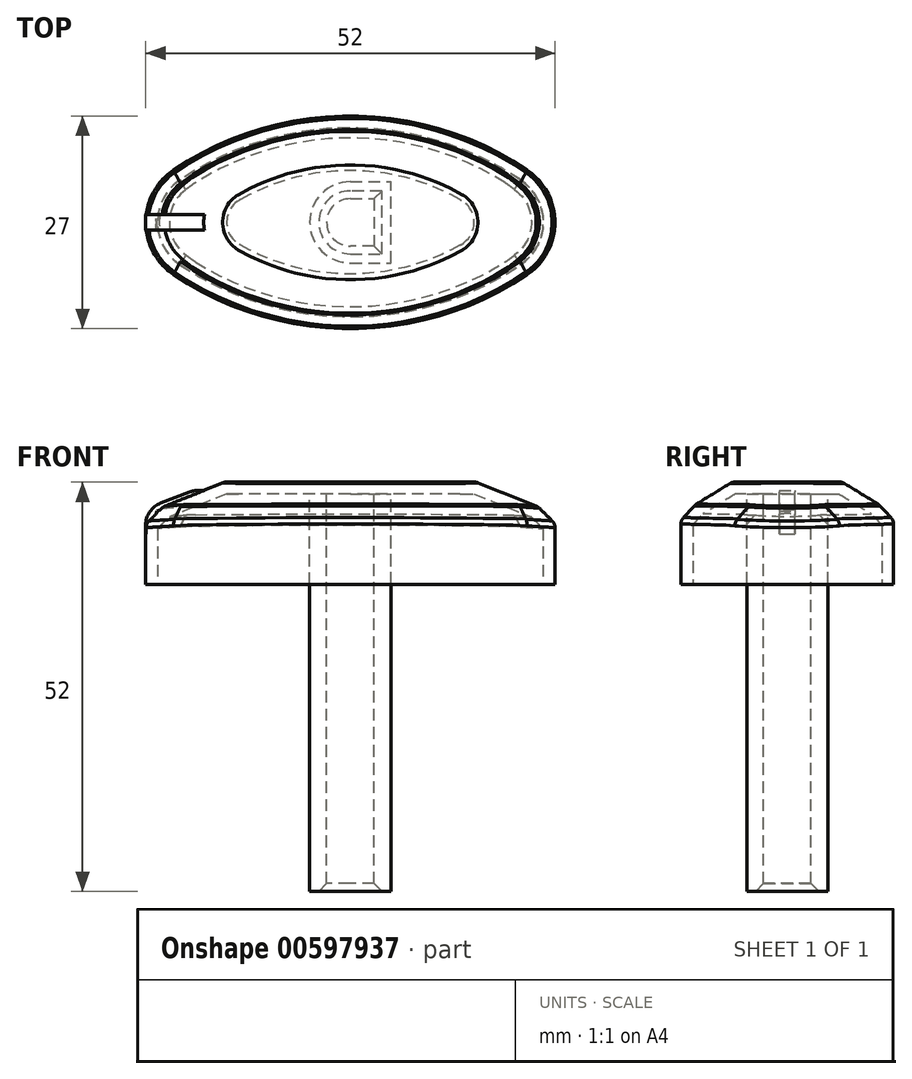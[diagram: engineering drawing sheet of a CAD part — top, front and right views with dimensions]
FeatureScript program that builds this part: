
annotation { "Feature Type Name" : "Feature", "Feature Type Description" : "" }
export const myFeature = defineFeature(function(context is Context, id is Id, definition is map)
    precondition{}
    {
        {
            var Q0;
            Q0=qCreatedBy(makeId("Top.planeOp"),FACE);
            var sketch = newSketch(context, id + "F0", { "sketchPlane" : qUnion([Q0])});
            skLineSegment(sketch, "E0.bottom", {"start": v(26, -13.5) * mm, "end": v(-26, -13.5) * mm, "construction": true});
            skLineSegment(sketch, "E0.top", {"start": v(26, 13.5) * mm, "end": v(-26, 13.5) * mm, "construction": true});
            skLineSegment(sketch, "E0.left", {"start": v(26, -13.5) * mm, "end": v(26, 13.5) * mm, "construction": true});
            skLineSegment(sketch, "E0.right", {"start": v(-26, -13.5) * mm, "end": v(-26, 13.5) * mm, "construction": true});
            skPoint(sketch, "E0.middle", {"position": v(0, 0) * mm});
            skCircle(sketch, "E1", {"center": v(-18, 0) * mm, "radius": 8 * mm});
            skPoint(sketch, "E1.centerSnap0", {"position": v(-26, 0) * mm});
            skCircle(sketch, "E2.MirrorC", {"center": v(18, 0) * mm, "radius": 8 * mm});
            skArc(sketch, "E3", {"start": v(22.47, 6.63) * mm, "mid": v(0, 13.5) * mm, "end": v(-22.47, 6.63) * mm});
            skArc(sketch, "E4.MirrorCS", {"start": v(22.47, -6.63) * mm, "mid": v(0, -13.5) * mm, "end": v(-22.47, -6.63) * mm});
            skSolve(sketch);
        }
        {
            var Q0;
            Q0 = qSketchRegion(id + "F0", true);
            extrude(context, id + "F1", {"entities" : qUnion([Q0]), "depth" : 9 * mm, "offsetDistance" : 25 * mm});
        }
        {
            var Q0;
            Q0=qCreatedBy(makeId("Top.planeOp"),FACE);
            cPlane(context, id + "F2", {"entities" : qUnion([Q0]), "cplaneType" : CPlaneType.OFFSET, "offset" : 13 * mm, "width" : 150 * mm, "height" : 150 * mm});
        }
        {
            var Q0;
            Q0=qCreatedBy(id+"F2.planeOp",FACE);
            var sketch = newSketch(context, id + "F3", { "sketchPlane" : qUnion([Q0])});
            skLineSegment(sketch, "E5.bottom", {"start": v(16, -7) * mm, "end": v(-16, -7) * mm, "construction": true});
            skLineSegment(sketch, "E5.top", {"start": v(16, 7) * mm, "end": v(-16, 7) * mm, "construction": true});
            skLineSegment(sketch, "E5.left", {"start": v(16, -7) * mm, "end": v(16, 7) * mm, "construction": true});
            skLineSegment(sketch, "E5.right", {"start": v(-16, -7) * mm, "end": v(-16, 7) * mm, "construction": true});
            skPoint(sketch, "E5.middle", {"position": v(0, 0) * mm});
            skArc(sketch, "E6", {"start": v(-14.1, 3.26) * mm, "mid": v(-16, 0) * mm, "end": v(-14.1, -3.26) * mm});
            skPoint(sketch, "E6.centerSnap0", {"position": v(-16, 0) * mm});
            skArc(sketch, "E7.MirrorC", {"start": v(14.1, 3.26) * mm, "mid": v(16, 0) * mm, "end": v(14.1, -3.26) * mm});
            skArc(sketch, "E8", {"start": v(14.1, 3.26) * mm, "mid": v(0, 7) * mm, "end": v(-14.1, 3.26) * mm});
            skArc(sketch, "E9.MirrorCS", {"start": v(14.1, -3.26) * mm, "mid": v(0, -7) * mm, "end": v(-14.1, -3.26) * mm});
            skSolve(sketch);
        }
        {
            var Q1;
            Q1=makeQuery(id+"F3.imprint","IMPRINT",FACE,{"disambiguationData":[TD([[makeQuery(id+"F3.imprint","IMPRINT",EDGE,{"derivedFrom":sQuery(id+"F3.wireOp",EDGE,"E6")}),1.0]])]});
            var Q2;
            Q2=makeQuery(id+"F1.opExtrude","CAP_FACE",FACE,{"disambiguationData":[OSD([sQuery(id+"F0.wireOp",EDGE,"E1"),sQuery(id+"F0.wireOp",EDGE,"E2.MirrorC"),sQuery(id+"F0.wireOp",EDGE,"E3"),sQuery(id+"F0.wireOp",EDGE,"E4.MirrorCS")])],"isStart":false});
            loft(context, id + "F4", {"operationType" : NewBodyOperationType.ADD, "sheetProfilesArray" : [{ "sheetProfileEntities" : qUnion([Q1]) }, { "sheetProfileEntities" : qUnion([Q2]) }]});
        }
        {
            var Q0;
            {var subQ0=sQuery(id+"F0.wireOp",EDGE,"E4.MirrorCS");Q0=makeQuery(id+"F4.boolean.opBoolean","MERGE",EDGE,{"derivedFrom":[makeQuery(id+"F1.opExtrude","CAP_EDGE",EDGE,{"disambiguationData":[OSD([subQ0])],"isStart":false}),makeQuery(id+"F4.opLoft","MID_CAP_EDGE",EDGE,{"disambiguationData":[OSD([sQuery(id+"F0.wireOp",EDGE,"E1"),sQuery(id+"F0.wireOp",EDGE,"E2.MirrorC"),subQ0])],"capPos":1.0})]});}
            chamfer(context, id + "F5", {"entities" : qUnion([Q0]), "chamferType" : ChamferType.TWO_OFFSETS, "width1" : 2.2 * mm, "oppositeDirection" : false, "width2" : 1 * mm, "tangentPropagation" : true});
        }
        {
            var Q0;
            {var subQ0=sQuery(id+"F0.wireOp",EDGE,"E2.MirrorC");var subQ1=sQuery(id+"F0.wireOp",EDGE,"E1");var subQ2=sQuery(id+"F0.wireOp",EDGE,"E4.MirrorCS");Q0=makeQuery(id+"F5.opChamfer","BLEND_EDGE",EDGE,{"blendedFrom":[makeQuery(id+"F4.boolean.opBoolean","MERGE",EDGE,{"derivedFrom":[makeQuery(id+"F1.opExtrude","CAP_EDGE",EDGE,{"disambiguationData":[OSD([subQ2])],"isStart":false}),makeQuery(id+"F4.opLoft","MID_CAP_EDGE",EDGE,{"disambiguationData":[OSD([subQ1,subQ0,subQ2])],"capPos":1.0})]}),makeQuery(id+"F4.opLoft","SWEPT_FACE",FACE,{"disambiguationData":[OSD([subQ1,subQ0,sQuery(id+"F0.wireOp",EDGE,"E3"),sQuery(id+"F3.wireOp",EDGE,"E6"),sQuery(id+"F3.wireOp",EDGE,"E7.MirrorC"),sQuery(id+"F3.wireOp",EDGE,"E8")])]})],"blendedInto":[makeQuery(id+"F4.opLoft","SWEPT_FACE",FACE,{"disambiguationData":[OSD([subQ1,subQ0,sQuery(id+"F0.wireOp",EDGE,"E3"),sQuery(id+"F3.wireOp",EDGE,"E6"),sQuery(id+"F3.wireOp",EDGE,"E7.MirrorC"),sQuery(id+"F3.wireOp",EDGE,"E8")])]})]});}
            var Q1;
            {var subQ0=sQuery(id+"F0.wireOp",EDGE,"E4.MirrorCS");Q1=makeQuery(id+"F5.opChamfer","BLEND_EDGE",EDGE,{"blendedFrom":[makeQuery(id+"F4.boolean.opBoolean","MERGE",EDGE,{"derivedFrom":[makeQuery(id+"F1.opExtrude","CAP_EDGE",EDGE,{"disambiguationData":[OSD([subQ0])],"isStart":false}),makeQuery(id+"F4.opLoft","MID_CAP_EDGE",EDGE,{"disambiguationData":[OSD([sQuery(id+"F0.wireOp",EDGE,"E1"),sQuery(id+"F0.wireOp",EDGE,"E2.MirrorC"),subQ0])],"capPos":1.0})]}),makeQuery(id+"F1.opExtrude","SWEPT_FACE",FACE,{"disambiguationData":[OSD([subQ0])]})],"blendedInto":[makeQuery(id+"F1.opExtrude","SWEPT_FACE",FACE,{"disambiguationData":[OSD([subQ0])]})]});}
            var Q2;
            Q2=makeQuery(id+"F4.opLoft","MID_CAP_EDGE",EDGE,{"disambiguationData":[OSD([sQuery(id+"F3.wireOp",EDGE,"E6"),sQuery(id+"F3.wireOp",EDGE,"E7.MirrorC"),sQuery(id+"F3.wireOp",EDGE,"E9.MirrorCS")])],"capPos":0.0});
            var Q3;
            {var subQ0=sQuery(id+"F0.wireOp",EDGE,"E3");var subQ1=sQuery(id+"F0.wireOp",EDGE,"E1");Q3=makeQuery(id+"F5.opChamfer","BLEND_EDGE",EDGE,{"blendedFrom":[makeQuery(id+"F4.boolean.opBoolean","MERGE",EDGE,{"derivedFrom":[makeQuery(id+"F1.opExtrude","CAP_EDGE",EDGE,{"disambiguationData":[OSD([subQ1])],"isStart":false}),makeQuery(id+"F4.opLoft","MID_CAP_EDGE",EDGE,{"disambiguationData":[OSD([subQ1,subQ0,sQuery(id+"F0.wireOp",EDGE,"E4.MirrorCS")])],"capPos":1.0})]}),makeQuery(id+"F4.opLoft","SWEPT_FACE",FACE,{"disambiguationData":[OSD([subQ1,sQuery(id+"F0.wireOp",EDGE,"E2.MirrorC"),subQ0,sQuery(id+"F3.wireOp",EDGE,"E6"),sQuery(id+"F3.wireOp",EDGE,"E7.MirrorC"),sQuery(id+"F3.wireOp",EDGE,"E8")])]})],"blendedInto":[makeQuery(id+"F4.opLoft","SWEPT_FACE",FACE,{"disambiguationData":[OSD([subQ1,sQuery(id+"F0.wireOp",EDGE,"E2.MirrorC"),subQ0,sQuery(id+"F3.wireOp",EDGE,"E6"),sQuery(id+"F3.wireOp",EDGE,"E7.MirrorC"),sQuery(id+"F3.wireOp",EDGE,"E8")])]})]});}
            var Q4;
            {var subQ0=sQuery(id+"F0.wireOp",EDGE,"E1");Q4=makeQuery(id+"F5.opChamfer","BLEND_EDGE",EDGE,{"blendedFrom":[makeQuery(id+"F4.boolean.opBoolean","MERGE",EDGE,{"derivedFrom":[makeQuery(id+"F1.opExtrude","CAP_EDGE",EDGE,{"disambiguationData":[OSD([subQ0])],"isStart":false}),makeQuery(id+"F4.opLoft","MID_CAP_EDGE",EDGE,{"disambiguationData":[OSD([subQ0,sQuery(id+"F0.wireOp",EDGE,"E3"),sQuery(id+"F0.wireOp",EDGE,"E4.MirrorCS")])],"capPos":1.0})]}),makeQuery(id+"F1.opExtrude","SWEPT_FACE",FACE,{"disambiguationData":[OSD([subQ0])]})],"blendedInto":[makeQuery(id+"F1.opExtrude","SWEPT_FACE",FACE,{"disambiguationData":[OSD([subQ0])]})]});}
            var Q5;
            {var subQ0=sQuery(id+"F0.wireOp",EDGE,"E3");var subQ1=sQuery(id+"F0.wireOp",EDGE,"E2.MirrorC");Q5=makeQuery(id+"F5.opChamfer","BLEND_EDGE",EDGE,{"blendedFrom":[makeQuery(id+"F4.boolean.opBoolean","MERGE",EDGE,{"derivedFrom":[makeQuery(id+"F1.opExtrude","CAP_EDGE",EDGE,{"disambiguationData":[OSD([subQ1])],"isStart":false}),makeQuery(id+"F4.opLoft","MID_CAP_EDGE",EDGE,{"disambiguationData":[OSD([subQ1,subQ0,sQuery(id+"F0.wireOp",EDGE,"E4.MirrorCS")])],"capPos":1.0})]}),makeQuery(id+"F4.opLoft","SWEPT_FACE",FACE,{"disambiguationData":[OSD([sQuery(id+"F0.wireOp",EDGE,"E1"),subQ1,subQ0,sQuery(id+"F3.wireOp",EDGE,"E6"),sQuery(id+"F3.wireOp",EDGE,"E7.MirrorC"),sQuery(id+"F3.wireOp",EDGE,"E8")])]})],"blendedInto":[makeQuery(id+"F4.opLoft","SWEPT_FACE",FACE,{"disambiguationData":[OSD([sQuery(id+"F0.wireOp",EDGE,"E1"),subQ1,subQ0,sQuery(id+"F3.wireOp",EDGE,"E6"),sQuery(id+"F3.wireOp",EDGE,"E7.MirrorC"),sQuery(id+"F3.wireOp",EDGE,"E8")])]})]});}
            var Q6;
            {var subQ0=sQuery(id+"F0.wireOp",EDGE,"E2.MirrorC");Q6=makeQuery(id+"F5.opChamfer","BLEND_EDGE",EDGE,{"blendedFrom":[makeQuery(id+"F4.boolean.opBoolean","MERGE",EDGE,{"derivedFrom":[makeQuery(id+"F1.opExtrude","CAP_EDGE",EDGE,{"disambiguationData":[OSD([subQ0])],"isStart":false}),makeQuery(id+"F4.opLoft","MID_CAP_EDGE",EDGE,{"disambiguationData":[OSD([subQ0,sQuery(id+"F0.wireOp",EDGE,"E3"),sQuery(id+"F0.wireOp",EDGE,"E4.MirrorCS")])],"capPos":1.0})]}),makeQuery(id+"F1.opExtrude","SWEPT_FACE",FACE,{"disambiguationData":[OSD([subQ0])]})],"blendedInto":[makeQuery(id+"F1.opExtrude","SWEPT_FACE",FACE,{"disambiguationData":[OSD([subQ0])]})]});}
            var Q7;
            {var subQ0=sQuery(id+"F0.wireOp",EDGE,"E3");var subQ1=sQuery(id+"F0.wireOp",EDGE,"E2.MirrorC");var subQ2=sQuery(id+"F0.wireOp",EDGE,"E1");Q7=makeQuery(id+"F5.opChamfer","BLEND_EDGE",EDGE,{"blendedFrom":[makeQuery(id+"F4.boolean.opBoolean","MERGE",EDGE,{"derivedFrom":[makeQuery(id+"F1.opExtrude","CAP_EDGE",EDGE,{"disambiguationData":[OSD([subQ0])],"isStart":false}),makeQuery(id+"F4.opLoft","MID_CAP_EDGE",EDGE,{"disambiguationData":[OSD([subQ2,subQ1,subQ0])],"capPos":1.0})]}),makeQuery(id+"F4.opLoft","SWEPT_FACE",FACE,{"disambiguationData":[OSD([subQ2,subQ1,subQ0,sQuery(id+"F3.wireOp",EDGE,"E6"),sQuery(id+"F3.wireOp",EDGE,"E7.MirrorC"),sQuery(id+"F3.wireOp",EDGE,"E8")])]})],"blendedInto":[makeQuery(id+"F4.opLoft","SWEPT_FACE",FACE,{"disambiguationData":[OSD([subQ2,subQ1,subQ0,sQuery(id+"F3.wireOp",EDGE,"E6"),sQuery(id+"F3.wireOp",EDGE,"E7.MirrorC"),sQuery(id+"F3.wireOp",EDGE,"E8")])]})]});}
            var Q8;
            {var subQ0=sQuery(id+"F0.wireOp",EDGE,"E3");Q8=makeQuery(id+"F5.opChamfer","BLEND_EDGE",EDGE,{"blendedFrom":[makeQuery(id+"F4.boolean.opBoolean","MERGE",EDGE,{"derivedFrom":[makeQuery(id+"F1.opExtrude","CAP_EDGE",EDGE,{"disambiguationData":[OSD([subQ0])],"isStart":false}),makeQuery(id+"F4.opLoft","MID_CAP_EDGE",EDGE,{"disambiguationData":[OSD([sQuery(id+"F0.wireOp",EDGE,"E1"),sQuery(id+"F0.wireOp",EDGE,"E2.MirrorC"),subQ0])],"capPos":1.0})]}),makeQuery(id+"F1.opExtrude","SWEPT_FACE",FACE,{"disambiguationData":[OSD([subQ0])]})],"blendedInto":[makeQuery(id+"F1.opExtrude","SWEPT_FACE",FACE,{"disambiguationData":[OSD([subQ0])]})]});}
            fillet(context, id + "F6", {"entities" : qUnion([Q0, Q1, Q2, Q3, Q4, Q5, Q6, Q7, Q8]), "radius" : 1.2 * mm, "tangentPropagation" : true, "allowEdgeOverflow" : false});
        }
        {
            var Q0;
            Q0=makeQuery(id+"F1.opExtrude","CAP_FACE",FACE,{"disambiguationData":[OSD([sQuery(id+"F0.wireOp",EDGE,"E1"),sQuery(id+"F0.wireOp",EDGE,"E2.MirrorC"),sQuery(id+"F0.wireOp",EDGE,"E3"),sQuery(id+"F0.wireOp",EDGE,"E4.MirrorCS")])],"isStart":true});
            shell(context, id + "F7", {"entities" : qUnion([Q0]), "thickness" : 1.5 * mm});
        }
        {
            var Q0;
            Q0=makeQuery(id+"F7.opShell","OFFSET_FACE",FACE,{"disambiguationData":[OSD([makeQuery(id+"F3.imprint","IMPRINT",FACE,{"disambiguationData":[TD([[makeQuery(id+"F3.imprint","IMPRINT",EDGE,{"derivedFrom":sQuery(id+"F3.wireOp",EDGE,"E6")}),1.0]])]})])]});
            var sketch = newSketch(context, id + "F8", { "sketchPlane" : qUnion([Q0])});
            skArc(sketch, "E10", {"start": v(0, 5.15) * mm, "mid": v(-5.15, 0) * mm, "end": v(0, -5.15) * mm});
            skArc(sketch, "E11", {"start": v(0, 3) * mm, "mid": v(-3, 0) * mm, "end": v(0, -3) * mm});
            skLineSegment(sketch, "E12.bottom", {"start": v(0, 5.15) * mm, "end": v(5.18, 5.15) * mm});
            skLineSegment(sketch, "E12.top", {"start": v(0, -5.15) * mm, "end": v(5.18, -5.15) * mm});
            skLineSegment(sketch, "E12.right", {"start": v(5.18, 5.15) * mm, "end": v(5.18, -5.15) * mm});
            skLineSegment(sketch, "E13.bottom", {"start": v(5.18, 5.15) * mm, "end": v(3.02, 5.15) * mm});
            skLineSegment(sketch, "E13.top", {"start": v(5.18, -5.15) * mm, "end": v(3.02, -5.15) * mm});
            skLineSegment(sketch, "E13.right", {"start": v(3.02, 3) * mm, "end": v(3.02, -3) * mm});
            skLineSegment(sketch, "E14.top", {"start": v(0, 3) * mm, "end": v(3.02, 3) * mm});
            skLineSegment(sketch, "E14.right", {"start": v(5.18, 5.15) * mm, "end": v(5.18, 3) * mm});
            skLineSegment(sketch, "E15.MirrorCS", {"start": v(0, -3) * mm, "end": v(3.02, -3) * mm});
            skPoint(sketch, "E16.orphan", {"position": v(5.18, -3) * mm});
            skSolve(sketch);
        }
        {
            var Q0;
            Q0 = qSketchRegion(id + "F8", true);
            extrude(context, id + "F9", {"entities" : qUnion([Q0]), "operationType" : NewBodyOperationType.ADD, "depth" : 50.5 * mm, "offsetDistance" : 25 * mm});
        }
        {
            var Q0;
            Q0=makeQuery(id+"F9.opExtrude","CAP_EDGE",EDGE,{"disambiguationData":[OSD([sQuery(id+"F8.wireOp",EDGE,"E10")])],"isStart":true});
            var Q1;
            Q1=makeQuery(id+"F9.opExtrude","CAP_EDGE",EDGE,{"disambiguationData":[OSD([sQuery(id+"F8.wireOp",EDGE,"E12.right"),sQuery(id+"F8.wireOp",EDGE,"E14.right")])],"isStart":true});
            var Q2;
            Q2=makeQuery(id+"F9.opExtrude","CAP_EDGE",EDGE,{"disambiguationData":[OSD([sQuery(id+"F8.wireOp",EDGE,"E11")])],"isStart":false});
            var Q3;
            Q3=makeQuery(id+"F9.opExtrude","CAP_EDGE",EDGE,{"disambiguationData":[OSD([sQuery(id+"F8.wireOp",EDGE,"E13.right")])],"isStart":false});
            chamfer(context, id + "F10", {"entities" : qUnion([Q0, Q1, Q2, Q3]), "width" : 1 * mm, "tangentPropagation" : true});
        }
        {
            var Q0;
            Q0=qCreatedBy(makeId("Front.planeOp"),FACE);
            var sketch = newSketch(context, id + "F11", { "sketchPlane" : qUnion([Q0])});
            skLineSegment(sketch, "E17", {"start": v(-26, 6.42) * mm, "end": v(-26, 9.6) * mm});
            skLineSegment(sketch, "E18", {"start": v(-26, 9.6) * mm, "end": v(-19.87, 11.95) * mm});
            skLineSegment(sketch, "E19", {"start": v(-19.87, 11.95) * mm, "end": v(-18.22, 11.95) * mm});
            skLineSegment(sketch, "E20", {"start": v(-18.22, 11.95) * mm, "end": v(-24.53, 9.32) * mm});
            skLineSegment(sketch, "E21", {"start": v(-24.53, 9.32) * mm, "end": v(-25.76, 6.44) * mm});
            skLineSegment(sketch, "E22", {"start": v(-25.76, 6.44) * mm, "end": v(-26, 6.42) * mm});
            skSolve(sketch);
        }
        {
            var Q0;
            Q0 = qSketchRegion(id + "F11", true);
            extrude(context, id + "F12", {"entities" : qUnion([Q0]), "operationType" : NewBodyOperationType.ADD, "endBound" : BoundingType.SYMMETRIC, "depth" : 2 * mm, "offsetDistance" : 25 * mm});
        }
        {
            var Q0;
            Q0=makeQuery(id+"F12.opExtrude","SWEPT_EDGE",EDGE,{"disambiguationData":[OSD([sQuery(id+"F11.wireOp",EDGE,"E17"),sQuery(id+"F11.wireOp",EDGE,"E18")])]});
            var Q1;
            Q1=makeQuery(id+"F12.opExtrude","SWEPT_EDGE",EDGE,{"disambiguationData":[OSD([sQuery(id+"F11.wireOp",EDGE,"E18"),sQuery(id+"F11.wireOp",EDGE,"E19")])]});
            fillet(context, id + "F13", {"entities" : qUnion([Q0, Q1]), "radius" : 3 * mm, "tangentPropagation" : true, "allowEdgeOverflow" : false});
        }
    });
